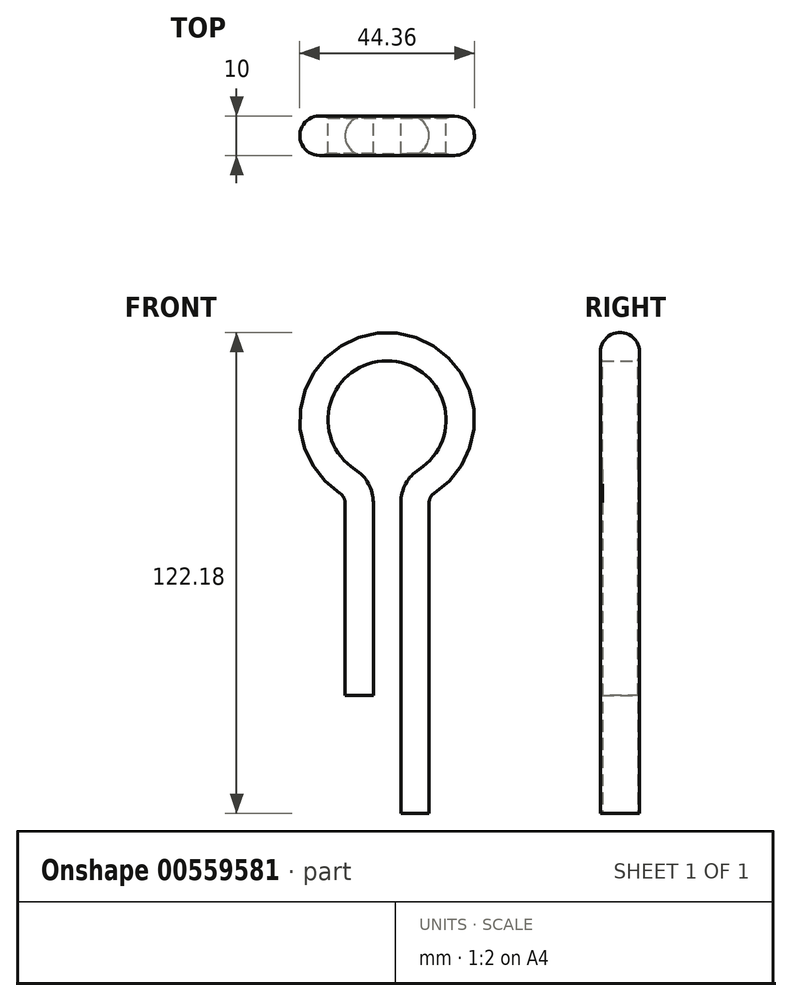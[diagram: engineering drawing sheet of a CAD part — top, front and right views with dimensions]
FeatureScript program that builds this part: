
annotation { "Feature Type Name" : "Feature", "Feature Type Description" : "" }
export const myFeature = defineFeature(function(context is Context, id is Id, definition is map)
    precondition{}
    {
        {
            var Q0;
            Q0=qCreatedBy(makeId("Front.planeOp"),FACE);
            var sketch = newSketch(context, id + "F0", { "sketchPlane" : qUnion([Q0])});
            skArc(sketch, "E0", {"start": v(8.1, -12.62) * mm, "mid": v(0, 15) * mm, "end": v(-8.1, -12.62) * mm});
            skLineSegment(sketch, "E1", {"start": v(3.5, -21.04) * mm, "end": v(3.5, -100) * mm});
            skLineSegment(sketch, "E2", {"start": v(-3.5, -21.04) * mm, "end": v(-3.5, -70) * mm});
            skArc(sketch, "E3", {"start": v(-3.5, -21.04) * mm, "mid": v(-4.73, -16.25) * mm, "end": v(-8.1, -12.62) * mm});
            skArc(sketch, "E4", {"start": v(3.5, -21.04) * mm, "mid": v(4.73, -16.25) * mm, "end": v(8.1, -12.62) * mm});
            skPoint(sketch, "E5.orphan", {"position": v(-3.5, 0) * mm});
            skPoint(sketch, "E6.orphan", {"position": v(3.5, 0) * mm});
            skSolve(sketch);
        }
        {
            var Q0;
            Q0=qCreatedBy(makeId("Top.planeOp"),FACE);
            cPlane(context, id + "F1", {"entities" : qUnion([Q0]), "cplaneType" : CPlaneType.OFFSET, "offset" : 70 * mm, "oppositeDirection" : true, "width" : 150 * mm, "height" : 150 * mm});
        }
        {
            var Q0;
            Q0=qCreatedBy(id+"F1.planeOp",FACE);
            var sketch = newSketch(context, id + "F2", { "sketchPlane" : qUnion([Q0])});
            skLineSegment(sketch, "E7", {"start": v(-3.5, -4.5) * mm, "end": v(-3.5, 4.5) * mm});
            skArc(sketch, "E8", {"start": v(-3.5, 4.5) * mm, "mid": v(-10.68, 0) * mm, "end": v(-3.5, -4.5) * mm});
            skSolve(sketch);
        }
        {
            var Q0;
            Q0=makeQuery(id+"F2.imprint","IMPRINT",FACE,{"disambiguationData":[TD([[makeQuery(id+"F2.imprint","IMPRINT",EDGE,{"derivedFrom":sQuery(id+"F2.wireOp",EDGE,"E7")}),1.0]])]});
            var Q1;
            Q1 = qConstructionFilter(qBodyType(qCreatedBy(id + "F0" ,EDGE), BodyType.WIRE), ConstructionObject.NO);
            sweep(context, id + "F3", {"profiles" : qUnion([Q0]), "path" : qUnion([Q1])});
        }
    });
